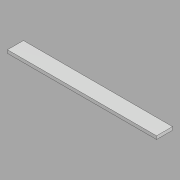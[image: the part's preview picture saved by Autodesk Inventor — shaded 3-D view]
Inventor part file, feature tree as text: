
AUTODESK INVENTOR PART (.ipt)
format: ipt  version: 2022.2 (Build 262287010, 287A)  size: 104,960 bytes
history: native  units: in
note: dims shown in document units (in); Inventor stores cm internally (conversion verified against a paired STEP export)
features: direct_edit x1, other x1, revolve x1
ambient origin geometry x8: Origin, YZ Plane, XZ Plane, XY Plane, X Axis, Y Axis, Z Axis, Center Point
bodies: Solid1 (feature_tree)
feature tree (3):
  direct_edit  "Direct Edit1"
  other  "R Vert rect jamb upper (3)"
  revolve  "Rotate1"  [1 undecoded]
note: 1 required parameter value undecoded (feature->parameter linkage not recoverable at this tier; creation-order binding heuristic only, values carry confidence <= 0.55)
